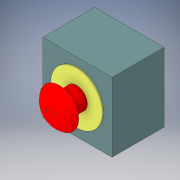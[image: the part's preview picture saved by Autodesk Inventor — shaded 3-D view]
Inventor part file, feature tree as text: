
AUTODESK INVENTOR PART (.ipt)
format: ipt  version: 2017 (Build 210142000, 142)  size: 152,576 bytes
history: native  units: in
note: dims shown in document units (in); Inventor stores cm internally (conversion verified against a paired STEP export)
features: extrude x4, sketch x4, fillet x1
ambient origin geometry x8: Origin, YZ Plane, XZ Plane, XY Plane, X Axis, Y Axis, Z Axis, Center Point
bodies: Solid1 (feature_tree)
feature tree (9):
  extrude  "Extrusion1"  Depth=3.1496in
  extrude  "Extrusion2"  Depth=2.3622in
  extrude  "Extrusion3"  Depth=2.3622in
  extrude  "Extrusion4"  Depth=0.7874in
  fillet  "Fillet1"  Radius=0.7874in
  sketch  "Sketch1"  dims[d0=3.1496in d1=3.1496in]
  sketch  "Sketch2"  dims[d2=2.3622in d3=0.0in d4=1.5748in]
  sketch  "Sketch3"  dims[d5=1.5748in d6=2.3622in]
  sketch  "Sketch4"  dims[d7=0.0394in d8=0.0in d9=0.9843in d10=0.7874in d11=0.0in d12=1.7717in d13=0.3937in d14=0.0in d15=0.7874in]
